# Revit family: Shower_System-Grohe-263790000
name_source: partatom
category: Plumbing Fixtures
revit_build: Autodesk Revit 2018 (Build: 20170223_1515(x64)
units: mm (PartAtom-declared; Revit-internal decimal feet)

## family parameters
Cut with Voids When Loaded = No
Host = Face
OmniClass Number = 23.45.05.14.17
OmniClass Title = Showers
Part Type = Normal
Room Calculation Point = No
Round Connector Dimension = Use Diameter
Shared = Yes

## types (1)
- 2637900000
    Assembly Code = D2010710
    Body Material = Metal-Grohe-000-StarLight Chrome
    CW Connection = Yes
    CWFU = 3
    Cold Water Connection Diameter = 1/2"
    Default Elevation = 0"
    Description = Shower System with Thermostat for Wall Mount
    Flow Rate = 2.5 GPM
    HW Connection = Yes
    HWFU = 3
    Height = 42 15/16"
    Hot Water Connection Diameter = 1/2"
    Installation Type = Wall-Mounted
    Length = 13 13/16"
    Manufacturer = Grohe
    Material = Metal-Grohe-000-StarLight Chrome
    Model = 26379000
    Price = Prices may vary. Please consult Manufacturer Representative for most up-to-date price list.
    Product Documentation Link = https://americanstandard.box.com
    Product Page URL = https://www.grohe.us
    URL = https://www.grohe.us
    Vent Connection = No
    WFU = 4
    Warranty Information = Limited Lifetime Warranty
    Waste Connection = No
    Width = 7 3/8"

## geometry (parser evidence)
native form markers: Sweep x3
no freeform markers — native parametric forms only
